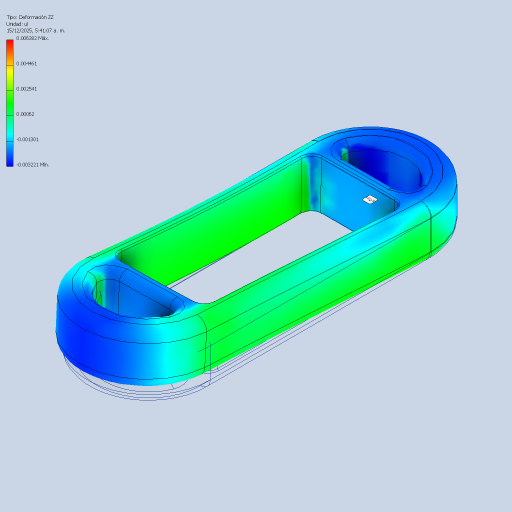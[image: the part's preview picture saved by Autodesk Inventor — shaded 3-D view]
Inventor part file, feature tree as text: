
AUTODESK INVENTOR PART (.ipt)
format: ipt  version: 2024 (Build 280153000, 153)  size: 569,344 bytes
history: native  units: mm
features: fillet x4, extrude x1, sketch x1
ambient origin geometry x8: Origin, YZ Plane, XZ Plane, XY Plane, X Axis, Y Axis, Z Axis, Center Point
bodies: Body1 (feature_tree)
feature tree (6):
  extrude  "Extrusión2"  Depth=10.0mm
  fillet  "Empalme2"  Radius=80.0mm
  fillet  "Empalme3"  Radius=38.0mm
  fillet  "Empalme4"  Radius=20.0mm
  fillet  "Empalme5"  Radius=4.0mm
  sketch  "Boceto1"  dims[d1=50.0mm d3=10.0mm d11=80.0mm d12=38.0mm d13=20.0mm d14=0.0mm d15=4.0mm d16=4.0mm d18=6.0mm d19=3.0mm d20=0.5mm]
